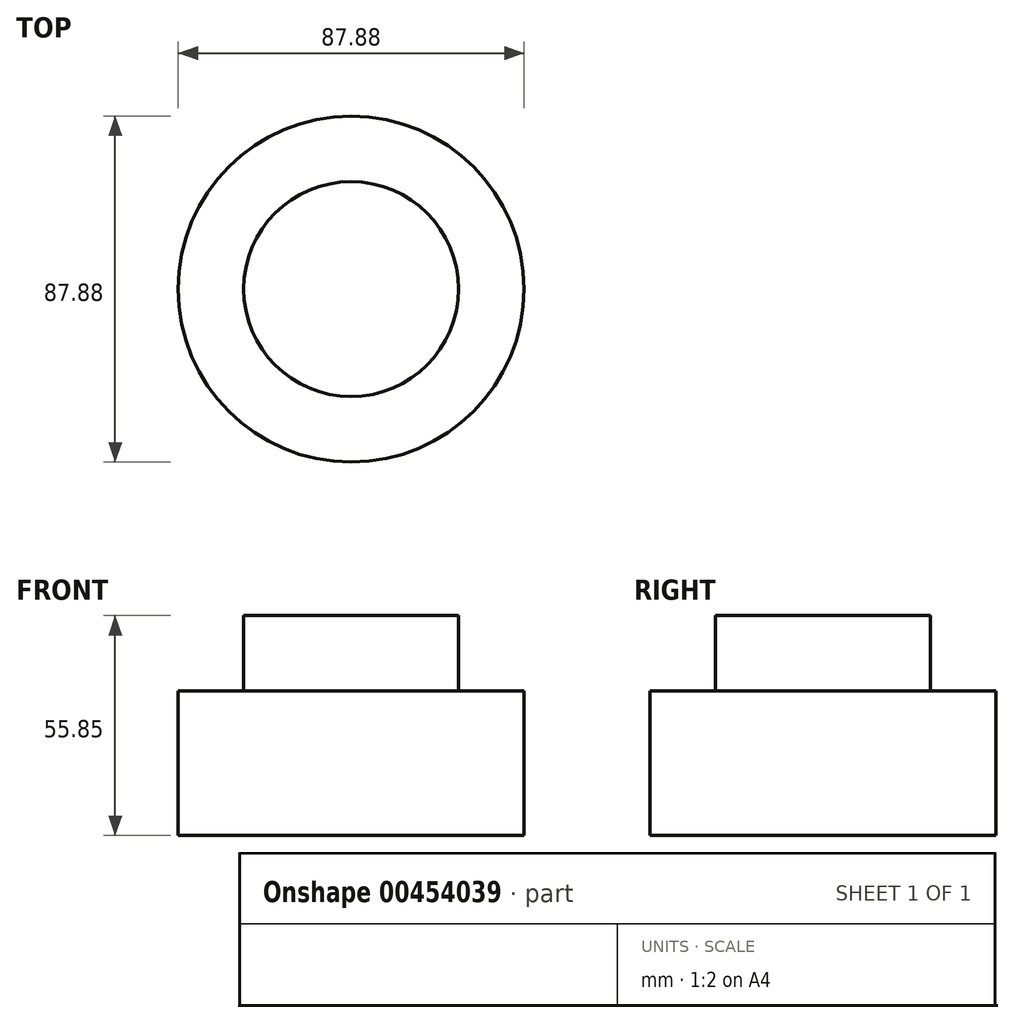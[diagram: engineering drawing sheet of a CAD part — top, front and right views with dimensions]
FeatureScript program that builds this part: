
annotation { "Feature Type Name" : "Feature", "Feature Type Description" : "" }
export const myFeature = defineFeature(function(context is Context, id is Id, definition is map)
    precondition{}
    {
        {
            var Q0;
            Q0=qCreatedBy(makeId("Front.planeOp"),FACE);
            var sketch = newSketch(context, id + "F0", { "sketchPlane" : qUnion([Q0])});
            skLineSegment(sketch, "E0.bottom", {"start": v(0, 0) * mm, "end": v(-43.94, 0) * mm});
            skLineSegment(sketch, "E0.top", {"start": v(0, 55.85) * mm, "end": v(-43.94, 55.85) * mm});
            skLineSegment(sketch, "E0.left", {"start": v(0, 0) * mm, "end": v(0, 55.85) * mm});
            skLineSegment(sketch, "E0.right", {"start": v(-43.94, 0) * mm, "end": v(-43.94, 55.85) * mm});
            skSolve(sketch);
        }
        {
            var Q0;
            Q0=makeQuery(id+"F0.imprint","IMPRINT",FACE,{"disambiguationData":[TD([[makeQuery(id+"F0.imprint","IMPRINT",EDGE,{"derivedFrom":sQuery(id+"F0.wireOp",EDGE,"E0.bottom")}),-1.0]])]});
            var Q1;
            Q1=sQuery(id+"F0.wireOp",EDGE,"E0.left");
            revolve(context, id + "F1", {"entities" : qUnion([Q0]), "axis" : qUnion([Q1]), "revolveType" : RevolveType.FULL});
        }
        {
            var Q0;
            Q0=qCreatedBy(makeId("Front.planeOp"),FACE);
            var sketch = newSketch(context, id + "F2", { "sketchPlane" : qUnion([Q0])});
            skLineSegment(sketch, "E1.bottom", {"start": v(-55.58, 56.85) * mm, "end": v(-27.29, 56.85) * mm});
            skLineSegment(sketch, "E1.top", {"start": v(-55.58, 36.63) * mm, "end": v(-27.29, 36.63) * mm});
            skLineSegment(sketch, "E1.left", {"start": v(-55.58, 56.85) * mm, "end": v(-55.58, 36.63) * mm});
            skLineSegment(sketch, "E1.right", {"start": v(-27.29, 56.85) * mm, "end": v(-27.29, 36.63) * mm});
            skLineSegment(sketch, "E2", {"start": v(0, 56.85) * mm, "end": v(0, 0) * mm});
            skPoint(sketch, "E2.startSnap0", {"position": v(-41.43, 56.85) * mm});
            skSolve(sketch);
        }
        {
            var Q0;
            Q0=makeQuery(id+"F2.imprint","IMPRINT",FACE,{"disambiguationData":[TD([[makeQuery(id+"F2.imprint","IMPRINT",EDGE,{"derivedFrom":sQuery(id+"F2.wireOp",EDGE,"E1.bottom")}),-1.0]])]});
            var Q1;
            Q1=sQuery(id+"F2.wireOp",EDGE,"E2");
            revolve(context, id + "F3", {"operationType" : NewBodyOperationType.REMOVE, "entities" : qUnion([Q0]), "axis" : qUnion([Q1]), "revolveType" : RevolveType.FULL, "oppositeDirection" : true});
        }
    });
